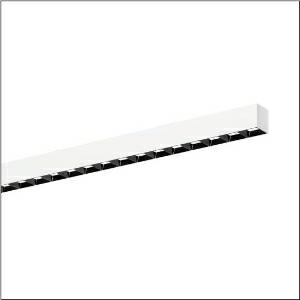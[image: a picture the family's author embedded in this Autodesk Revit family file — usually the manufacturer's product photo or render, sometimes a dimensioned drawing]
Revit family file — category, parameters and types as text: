
# Revit family: silica_r__21_51mx22tat4w_9510
name_source: partatom
category: Lighting Fixtures
units: mm (PartAtom-declared; Revit-internal decimal feet)

## family parameters
Cut with Voids When Loaded = No
Host = Face
Light Source = No
Part Type = Normal
Room Calculation Point = No
Round Connector Dimension = Use Diameter
Shared = No

## types (1)
- --- (1 x LED, 3720 lm, 32.1 W, 6500K)
    Apparent Load = 32 VA
    CIE Flux Codes = 84 100 100 100 100
    Color Rendering = 80
    Color Temperature = 6500K
    Default Elevation = 1800 mm
    Description = Silica® 21, office luminaire, primary light control with darklight reflector, of PMMA, black, CAT 2 (L<= 3000cd/m²), light emission: direct distribution, primary light characteristic: symmetric, installation type: surface-mounted, LED, rated luminous flux: 3.720lm, luminous efficacy: 110lm/W, light colour: 8tw, colour temperature: 2700..6500K, control gear: ECG DALI, with terminal, 3+2-pole, max. 2.5mm², mains connection: 220..240V, AC, 50/60Hz, rated input power: 33.8W, luminaire housing, of aluminium, traffic white (RAL 9016), length: 1.204mm, width: 53mm, height: 53mm, protection rating (complete): IP20, insulation class (complete): insulation class I (protective earthing), certification: CE, permissible operating ambient temperature: 0..+35°C, standard: EN 50419, packaging unit: 1 piece
    Height = 53 mm
    Lamp = 1 x LED
    Lamp Light Flux = 3720 lm
    Lamp Power = 32.1 W
    Lamp count = 1
    Length = 1204 mm
    Luminous efficacy = 116 lm/W
    Manufacturer = Siteco
    ModVariant = No
    Model = 51MX22TAT4W
    Mounting Place = Ceiling
    Mounting Type = Surface mounted
    Number of Poles = 1
    OnlyDefault = Yes
    Power Factor = 1
    Product Name = Silica® 21
    Product group = office luminaire | ceiling mounted
    ProductGroupID = 302
    Protection Class = Protection class I
    Protection Degree = IP 20
    RLX_Detail_Level = 1
    RlxData = <blob elided: 37809 chars, md5=465fd70f>
    Socket = socket
    Standby Power = 0 W
    System Light Flux = 3720 lm
    System Power = 32 W
    Type Comments = individual setting
    Type Image = l_1251676.jpg
    URL = http://relux.com
    VarID = @adj_046251
    Voltage = 0 V
    Weight = 0.00 kg
    Width = 53 mm

## geometry (parser evidence)
native form markers: Blend x4, Sweep x11
no freeform markers — native parametric forms only
